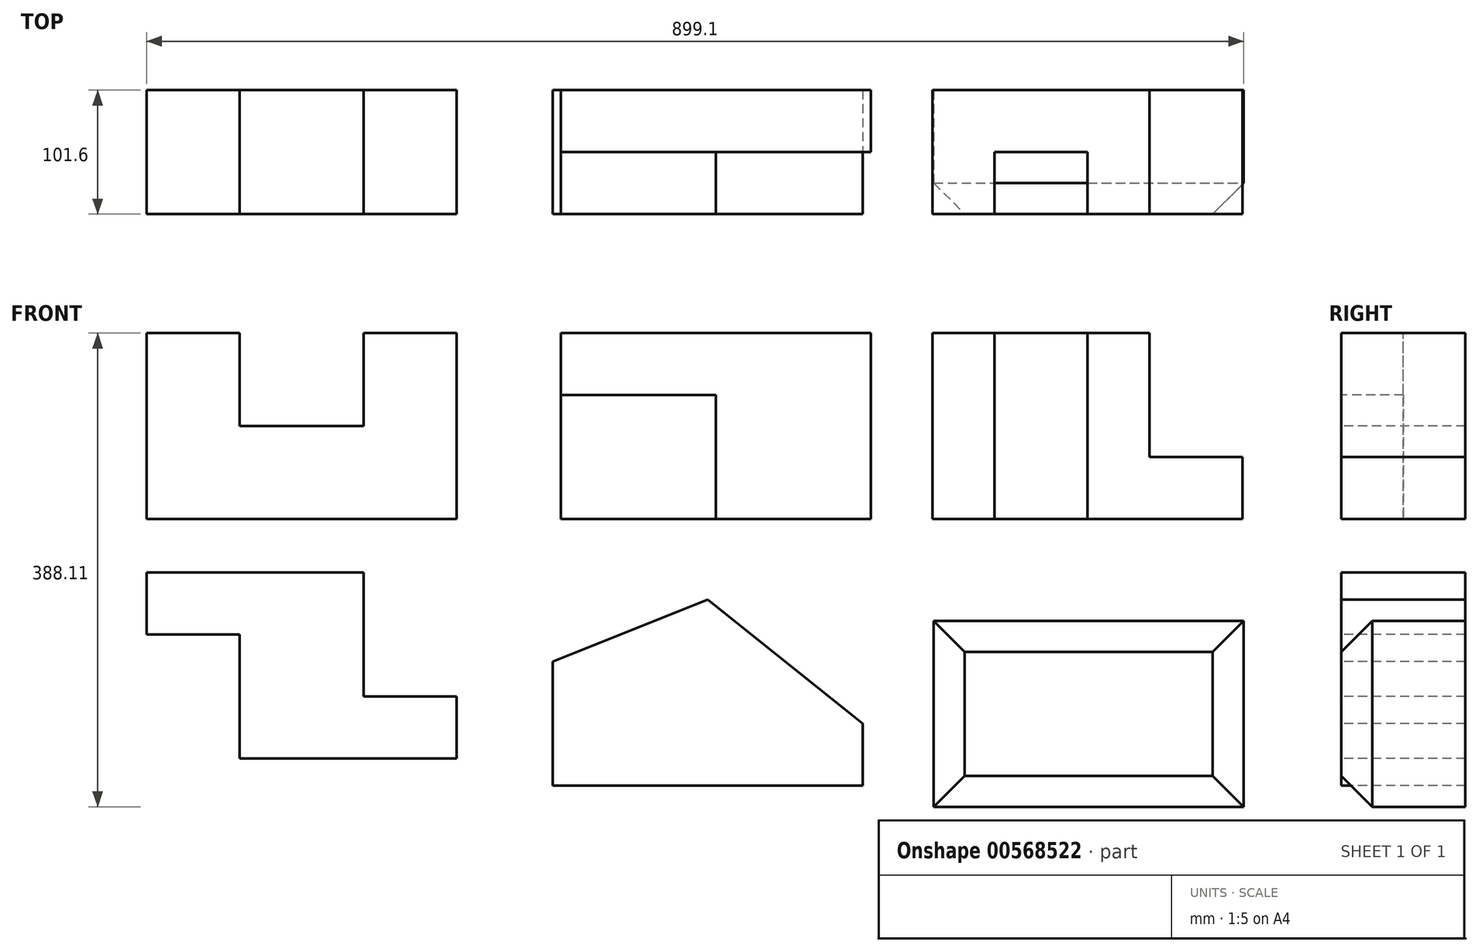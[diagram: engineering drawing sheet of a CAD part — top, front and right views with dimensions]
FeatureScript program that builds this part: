
annotation { "Feature Type Name" : "Feature", "Feature Type Description" : "" }
export const myFeature = defineFeature(function(context is Context, id is Id, definition is map)
    precondition{}
    {
        {
            var Q0;
            Q0=qCreatedBy(makeId("Front.planeOp"),FACE);
            var sketch = newSketch(context, id + "F0", { "sketchPlane" : qUnion([Q0])});
            skLineSegment(sketch, "E0", {"start": v(0, 0) * mm, "end": v(254, 0) * mm});
            skLineSegment(sketch, "E1", {"start": v(254, 0) * mm, "end": v(254, 152.4) * mm});
            skLineSegment(sketch, "E2", {"start": v(254, 152.4) * mm, "end": v(177.8, 152.4) * mm});
            skLineSegment(sketch, "E3", {"start": v(177.8, 152.4) * mm, "end": v(177.8, 76.2) * mm});
            skLineSegment(sketch, "E4", {"start": v(177.8, 76.2) * mm, "end": v(76.2, 76.2) * mm});
            skLineSegment(sketch, "E5", {"start": v(76.2, 76.2) * mm, "end": v(76.2, 152.4) * mm});
            skLineSegment(sketch, "E6", {"start": v(76.2, 152.4) * mm, "end": v(0, 152.4) * mm});
            skLineSegment(sketch, "E7", {"start": v(0, 152.4) * mm, "end": v(0, 0) * mm});
            skSolve(sketch);
        }
        {
            var Q0;
            Q0=makeQuery(id+"F0.imprint","IMPRINT",FACE,{"disambiguationData":[TD([[makeQuery(id+"F0.imprint","IMPRINT",EDGE,{"derivedFrom":sQuery(id+"F0.wireOp",EDGE,"E0")}),1.0]])]});
            extrude(context, id + "F1", {"entities" : qUnion([Q0]), "oppositeDirection" : true, "depth" : 101.6 * mm, "offsetDistance" : 25.4 * mm});
        }
        {
            var Q0;
            Q0=qCreatedBy(makeId("Front.planeOp"),FACE);
            var sketch = newSketch(context, id + "F2", { "sketchPlane" : qUnion([Q0])});
            skLineSegment(sketch, "E8.bottom", {"start": v(339.56, 0) * mm, "end": v(593.56, 0) * mm});
            skLineSegment(sketch, "E8.top", {"start": v(339.56, 152.4) * mm, "end": v(593.56, 152.4) * mm});
            skLineSegment(sketch, "E8.left", {"start": v(339.56, 0) * mm, "end": v(339.56, 152.4) * mm});
            skLineSegment(sketch, "E8.right", {"start": v(593.56, 0) * mm, "end": v(593.56, 152.4) * mm});
            skSolve(sketch);
        }
        {
            var Q0;
            Q0 = qSketchRegion(id + "F2", true);
            extrude(context, id + "F3", {"entities" : qUnion([Q0]), "oppositeDirection" : true, "depth" : 101.6 * mm, "offsetDistance" : 25.4 * mm});
        }
        {
            var Q0;
            Q0=makeQuery(id+"F3.opExtrude","CAP_FACE",FACE,{"disambiguationData":[OSD([sQuery(id+"F2.wireOp",EDGE,"E8.bottom"),sQuery(id+"F2.wireOp",EDGE,"E8.top"),sQuery(id+"F2.wireOp",EDGE,"E8.left"),sQuery(id+"F2.wireOp",EDGE,"E8.right")])],"isStart":true});
            var sketch = newSketch(context, id + "F4", { "sketchPlane" : qUnion([Q0])});
            skLineSegment(sketch, "E9", {"start": v(339.56, 101.6) * mm, "end": v(466.56, 101.6) * mm});
            skLineSegment(sketch, "E10", {"start": v(466.56, 101.6) * mm, "end": v(466.56, 0) * mm});
            skLineSegment(sketch, "E11", {"start": v(339.56, 152.4) * mm, "end": v(339.56, 101.6) * mm});
            skLineSegment(sketch, "E12", {"start": v(466.56, 0) * mm, "end": v(593.56, 0) * mm});
            skSolve(sketch);
        }
        {
            var Q0;
            Q0=makeQuery(id+"F4.imprint","IMPRINT",FACE,{"disambiguationData":[TD([[makeQuery(id+"F4.imprint","IMPRINT",EDGE,{"derivedFrom":sQuery(id+"F4.wireOp",EDGE,"E9")}),1.0]])]});
            extrude(context, id + "F5", {"entities" : qUnion([Q0]), "operationType" : NewBodyOperationType.REMOVE, "oppositeDirection" : true, "depth" : 50.8 * mm, "offsetDistance" : 25.4 * mm});
        }
        {
            var Q0;
            Q0=qCreatedBy(makeId("Front.planeOp"),FACE);
            var sketch = newSketch(context, id + "F6", { "sketchPlane" : qUnion([Q0])});
            skLineSegment(sketch, "E13", {"start": v(644.07, 0) * mm, "end": v(898.07, 0) * mm});
            skLineSegment(sketch, "E14", {"start": v(898.07, 0) * mm, "end": v(898.07, 50.8) * mm});
            skLineSegment(sketch, "E15", {"start": v(898.07, 50.8) * mm, "end": v(821.87, 50.8) * mm});
            skLineSegment(sketch, "E16", {"start": v(821.87, 50.8) * mm, "end": v(821.87, 152.4) * mm});
            skLineSegment(sketch, "E17", {"start": v(644.07, 0) * mm, "end": v(644.07, 152.4) * mm});
            skLineSegment(sketch, "E18", {"start": v(644.07, 152.4) * mm, "end": v(821.87, 152.4) * mm});
            skSolve(sketch);
        }
        {
            var Q0;
            Q0=makeQuery(id+"F6.imprint","IMPRINT",FACE,{"disambiguationData":[TD([[makeQuery(id+"F6.imprint","IMPRINT",EDGE,{"derivedFrom":sQuery(id+"F6.wireOp",EDGE,"E13")}),1.0]])]});
            extrude(context, id + "F7", {"entities" : qUnion([Q0]), "oppositeDirection" : true, "depth" : 101.6 * mm, "offsetDistance" : 25.4 * mm});
        }
        {
            var Q0;
            Q0=makeQuery(id+"F7.opExtrude","SWEPT_FACE",FACE,{"disambiguationData":[OSD([sQuery(id+"F6.wireOp",EDGE,"E18")])]});
            var sketch = newSketch(context, id + "F8", { "sketchPlane" : qUnion([Q0])});
            skLineSegment(sketch, "E19", {"start": v(644.07, 0) * mm, "end": v(694.87, 0) * mm});
            skLineSegment(sketch, "E20", {"start": v(694.87, 0) * mm, "end": v(694.87, 50.8) * mm});
            skLineSegment(sketch, "E21", {"start": v(694.87, 50.8) * mm, "end": v(771.07, 50.8) * mm});
            skLineSegment(sketch, "E22", {"start": v(771.07, 50.8) * mm, "end": v(771.07, 0) * mm});
            skLineSegment(sketch, "E23", {"start": v(771.07, 0) * mm, "end": v(821.87, 0) * mm});
            skSolve(sketch);
        }
        {
            var Q0;
            {var subQ0=sQuery(id+"F8.wireOp",EDGE,"E20");Q0=makeQuery(id+"F8.imprint","IMPRINT",FACE,{"disambiguationData":[TD([[makeQuery(id+"F8.imprint","IMPRINT",EDGE,{"derivedFrom":subQ0}),-1.0]])]});}
            extrude(context, id + "F9", {"entities" : qUnion([Q0]), "operationType" : NewBodyOperationType.REMOVE, "oppositeDirection" : true, "depth" : 152.4 * mm, "offsetDistance" : 25.4 * mm});
        }
        {
            var Q0;
            Q0=qCreatedBy(makeId("Front.planeOp"),FACE);
            var sketch = newSketch(context, id + "F10", { "sketchPlane" : qUnion([Q0])});
            skLineSegment(sketch, "E24", {"start": v(0, -43.85) * mm, "end": v(0, -94.65) * mm});
            skLineSegment(sketch, "E25", {"start": v(0, -94.65) * mm, "end": v(76.2, -94.65) * mm});
            skLineSegment(sketch, "E26", {"start": v(76.2, -94.65) * mm, "end": v(76.2, -196.25) * mm});
            skLineSegment(sketch, "E27", {"start": v(76.2, -196.25) * mm, "end": v(254, -196.25) * mm});
            skLineSegment(sketch, "E28", {"start": v(254, -196.25) * mm, "end": v(254, -145.45) * mm});
            skLineSegment(sketch, "E29", {"start": v(254, -145.45) * mm, "end": v(177.8, -145.45) * mm});
            skLineSegment(sketch, "E30", {"start": v(177.8, -145.45) * mm, "end": v(177.8, -43.85) * mm});
            skLineSegment(sketch, "E31", {"start": v(177.8, -43.85) * mm, "end": v(0, -43.85) * mm});
            skSolve(sketch);
        }
        {
            var Q0;
            Q0=makeQuery(id+"F10.imprint","IMPRINT",FACE,{"disambiguationData":[TD([[makeQuery(id+"F10.imprint","IMPRINT",EDGE,{"derivedFrom":sQuery(id+"F10.wireOp",EDGE,"E24")}),1.0]])]});
            extrude(context, id + "F11", {"entities" : qUnion([Q0]), "oppositeDirection" : true, "depth" : 101.6 * mm, "offsetDistance" : 25.4 * mm});
        }
        {
            var Q0;
            Q0=qCreatedBy(makeId("Front.planeOp"),FACE);
            var sketch = newSketch(context, id + "F12", { "sketchPlane" : qUnion([Q0])});
            skLineSegment(sketch, "E32.bottom", {"start": v(332.98, -66) * mm, "end": v(586.98, -66) * mm});
            skLineSegment(sketch, "E32.top", {"start": v(332.98, -218.4) * mm, "end": v(586.98, -218.4) * mm});
            skLineSegment(sketch, "E32.left", {"start": v(332.98, -66) * mm, "end": v(332.98, -218.4) * mm});
            skLineSegment(sketch, "E32.right", {"start": v(586.98, -66) * mm, "end": v(586.98, -218.4) * mm});
            skPoint(sketch, "E33", {"position": v(586.98, -167.6) * mm});
            skLineSegment(sketch, "E34", {"start": v(459.98, -66) * mm, "end": v(586.98, -167.6) * mm});
            skPoint(sketch, "E35", {"position": v(332.98, -116.8) * mm});
            skLineSegment(sketch, "E36", {"start": v(332.98, -116.8) * mm, "end": v(459.98, -66) * mm});
            skSolve(sketch);
        }
        {
            var Q0;
            Q0 = qSketchRegion(id + "F12", true);
            extrude(context, id + "F13", {"entities" : qUnion([Q0]), "oppositeDirection" : true, "depth" : 101.6 * mm, "offsetDistance" : 25.4 * mm});
        }
        {
            var Q0;
            Q0=makeQuery(id+"F13.opExtrude","CAP_FACE",FACE,{"disambiguationData":[OSD([sQuery(id+"F12.wireOp",EDGE,"E32.bottom"),sQuery(id+"F12.wireOp",EDGE,"E32.top"),sQuery(id+"F12.wireOp",EDGE,"E32.left"),sQuery(id+"F12.wireOp",EDGE,"E32.right")])],"isStart":true});
            var sketch = newSketch(context, id + "F14", { "sketchPlane" : qUnion([Q0])});
            skPoint(sketch, "E37", {"position": v(332.98, -116.8) * mm});
            skPoint(sketch, "E38", {"position": v(586.98, -167.6) * mm});
            skLineSegment(sketch, "E39", {"start": v(332.98, -116.8) * mm, "end": v(459.98, -66) * mm});
            skLineSegment(sketch, "E40", {"start": v(459.98, -66) * mm, "end": v(332.98, -66) * mm});
            skLineSegment(sketch, "E41", {"start": v(332.98, -66) * mm, "end": v(332.98, -116.8) * mm});
            skLineSegment(sketch, "E42", {"start": v(586.98, -167.6) * mm, "end": v(459.98, -66) * mm});
            skLineSegment(sketch, "E43", {"start": v(586.98, -66) * mm, "end": v(586.98, -167.6) * mm});
            skSolve(sketch);
        }
        {
            var Q0;
            Q0=makeQuery(id+"F14.imprint","IMPRINT",FACE,{"disambiguationData":[TD([[makeQuery(id+"F14.imprint","IMPRINT",EDGE,{"derivedFrom":sQuery(id+"F14.wireOp",EDGE,"E39")}),1.0]])]});
            extrude(context, id + "F15", {"entities" : qUnion([Q0]), "operationType" : NewBodyOperationType.REMOVE, "oppositeDirection" : true, "depth" : 101.6 * mm, "offsetDistance" : 25.4 * mm});
        }
        {
            var Q0;
            Q0=makeQuery(id+"F13.opExtrude","CAP_FACE",FACE,{"disambiguationData":[OSD([sQuery(id+"F12.wireOp",EDGE,"E32.bottom"),sQuery(id+"F12.wireOp",EDGE,"E32.top"),sQuery(id+"F12.wireOp",EDGE,"E32.left"),sQuery(id+"F12.wireOp",EDGE,"E32.right")])],"isStart":true});
            var sketch = newSketch(context, id + "F16", { "sketchPlane" : qUnion([Q0])});
            skPoint(sketch, "E44", {"position": v(586.98, -167.6) * mm});
            skLineSegment(sketch, "E45", {"start": v(586.98, -167.6) * mm, "end": v(459.98, -66) * mm});
            skLineSegment(sketch, "E46", {"start": v(459.98, -66) * mm, "end": v(586.98, -66) * mm});
            skLineSegment(sketch, "E47", {"start": v(586.98, -66) * mm, "end": v(586.98, -167.6) * mm});
            skSolve(sketch);
        }
        {
            var Q0;
            Q0=makeQuery(id+"F16.imprint","IMPRINT",FACE,{"disambiguationData":[TD([[makeQuery(id+"F16.imprint","IMPRINT",EDGE,{"derivedFrom":sQuery(id+"F16.wireOp",EDGE,"E45")}),-1.0]])]});
            extrude(context, id + "F17", {"entities" : qUnion([Q0]), "operationType" : NewBodyOperationType.REMOVE, "oppositeDirection" : true, "depth" : 101.6 * mm, "offsetDistance" : 25.4 * mm});
        }
        {
            var Q0;
            Q0=qCreatedBy(makeId("Front.planeOp"),FACE);
            var sketch = newSketch(context, id + "F18", { "sketchPlane" : qUnion([Q0])});
            skLineSegment(sketch, "E48.bottom", {"start": v(645.1, -83.3) * mm, "end": v(899.1, -83.3) * mm});
            skLineSegment(sketch, "E48.top", {"start": v(645.1, -235.7) * mm, "end": v(899.1, -235.7) * mm});
            skLineSegment(sketch, "E48.left", {"start": v(645.1, -83.3) * mm, "end": v(645.1, -235.7) * mm});
            skLineSegment(sketch, "E48.right", {"start": v(899.1, -83.3) * mm, "end": v(899.1, -235.7) * mm});
            skSolve(sketch);
        }
        {
            var Q0;
            Q0 = qSketchRegion(id + "F18", true);
            extrude(context, id + "F19", {"entities" : qUnion([Q0]), "oppositeDirection" : true, "depth" : 101.6 * mm, "offsetDistance" : 25.4 * mm});
        }
        {
            var Q0;
            Q0=makeQuery(id+"F19.opExtrude","SWEPT_FACE",FACE,{"disambiguationData":[OSD([sQuery(id+"F18.wireOp",EDGE,"E48.right")])]});
            var sketch = newSketch(context, id + "F20", { "sketchPlane" : qUnion([Q0])});
            skPoint(sketch, "E49", {"position": v(25.4, -235.7) * mm});
            skPoint(sketch, "E50", {"position": v(0, -210.3) * mm});
            skLineSegment(sketch, "E51", {"start": v(0, -210.3) * mm, "end": v(25.4, -235.7) * mm});
            skLineSegment(sketch, "E52", {"start": v(0, -210.3) * mm, "end": v(0, -235.7) * mm});
            skLineSegment(sketch, "E53", {"start": v(0, -235.7) * mm, "end": v(25.4, -235.7) * mm});
            skSolve(sketch);
        }
        {
            var Q0;
            Q0=makeQuery(id+"F20.imprint","IMPRINT",FACE,{"disambiguationData":[TD([[makeQuery(id+"F20.imprint","IMPRINT",EDGE,{"derivedFrom":sQuery(id+"F20.wireOp",EDGE,"E51")}),-1.0]])]});
            extrude(context, id + "F21", {"entities" : qUnion([Q0]), "operationType" : NewBodyOperationType.REMOVE, "oppositeDirection" : true, "depth" : 254 * mm, "offsetDistance" : 25.4 * mm});
        }
        {
            var Q0;
            Q0=makeQuery(id+"F19.opExtrude","SWEPT_FACE",FACE,{"disambiguationData":[OSD([sQuery(id+"F18.wireOp",EDGE,"E48.right")])]});
            var sketch = newSketch(context, id + "F22", { "sketchPlane" : qUnion([Q0])});
            skPoint(sketch, "E54", {"position": v(25.4, -83.3) * mm});
            skPoint(sketch, "E55", {"position": v(0, -108.7) * mm});
            skLineSegment(sketch, "E56", {"start": v(25.4, -83.3) * mm, "end": v(0, -108.7) * mm});
            skLineSegment(sketch, "E57", {"start": v(0, -83.3) * mm, "end": v(25.4, -83.3) * mm});
            skSolve(sketch);
        }
        {
            var Q0;
            {var subQ0=sQuery(id+"F22.wireOp",EDGE,"E56");Q0=makeQuery(id+"F22.imprint","IMPRINT",FACE,{"disambiguationData":[TD([[makeQuery(id+"F22.imprint","IMPRINT",EDGE,{"derivedFrom":subQ0}),-1.0]])]});}
            extrude(context, id + "F23", {"entities" : qUnion([Q0]), "operationType" : NewBodyOperationType.ADD, "depth" : 254 * mm, "offsetDistance" : 25.4 * mm});
        }
        {
            var Q0;
            Q0=makeQuery(id+"F23.opExtrude","CAP_FACE",FACE,{"disambiguationData":[OSD([sQuery(id+"F18.wireOp",EDGE,"E48.right"),sQuery(id+"F22.wireOp",EDGE,"E56"),sQuery(id+"F22.wireOp",EDGE,"E57")])],"isStart":false});
            extrude(context, id + "F24", {"entities" : qUnion([Q0]), "operationType" : NewBodyOperationType.REMOVE, "oppositeDirection" : true, "depth" : 508 * mm, "offsetDistance" : 25.4 * mm});
        }
        {
            var Q0;
            Q0=makeQuery(id+"F19.opExtrude","CAP_EDGE",EDGE,{"disambiguationData":[OSD([sQuery(id+"F18.wireOp",EDGE,"E48.right")])],"isStart":true});
            chamfer(context, id + "F25", {"entities" : qUnion([Q0]), "width" : 25.4 * mm, "tangentPropagation" : true});
        }
        {
            var Q0;
            Q0=makeQuery(id+"F19.opExtrude","CAP_EDGE",EDGE,{"disambiguationData":[OSD([sQuery(id+"F18.wireOp",EDGE,"E48.left")])],"isStart":true});
            chamfer(context, id + "F26", {"entities" : qUnion([Q0]), "width" : 25.4 * mm, "tangentPropagation" : true});
        }
    });
